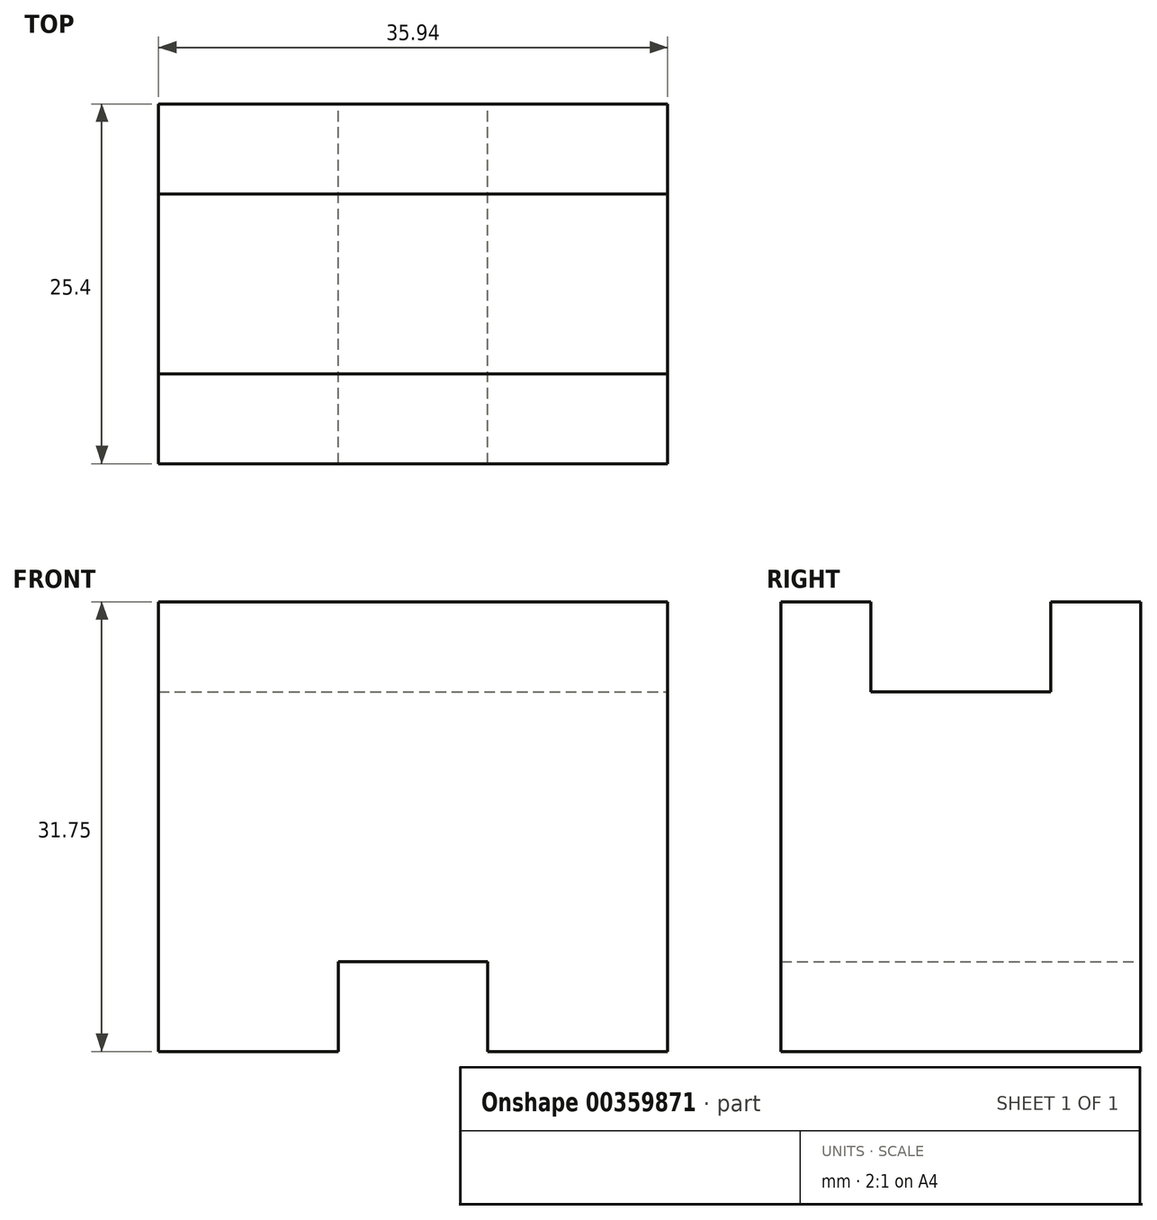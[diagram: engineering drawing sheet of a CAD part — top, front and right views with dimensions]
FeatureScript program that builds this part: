
annotation { "Feature Type Name" : "Feature", "Feature Type Description" : "" }
export const myFeature = defineFeature(function(context is Context, id is Id, definition is map)
    precondition{}
    {
        {
            var Q0;
            Q0=qCreatedBy(makeId("Front.planeOp"),FACE);
            var sketch = newSketch(context, id + "F0", { "sketchPlane" : qUnion([Q0])});
            skLineSegment(sketch, "E0", {"start": v(0, 0) * mm, "end": v(0, 31.75) * mm});
            skLineSegment(sketch, "E1", {"start": v(0, 31.75) * mm, "end": v(35.94, 31.75) * mm});
            skLineSegment(sketch, "E2", {"start": v(35.94, 31.75) * mm, "end": v(35.94, 0) * mm});
            skLineSegment(sketch, "E3", {"start": v(35.94, 0) * mm, "end": v(23.24, 0) * mm});
            skLineSegment(sketch, "E4", {"start": v(23.24, 0) * mm, "end": v(23.24, 6.35) * mm});
            skLineSegment(sketch, "E5", {"start": v(23.24, 6.35) * mm, "end": v(12.7, 6.35) * mm});
            skLineSegment(sketch, "E6", {"start": v(12.7, 6.35) * mm, "end": v(12.7, 0) * mm});
            skLineSegment(sketch, "E7", {"start": v(12.7, 0) * mm, "end": v(0, 0) * mm});
            skSolve(sketch);
        }
        {
            var Q0;
            Q0 = qSketchRegion(id + "F0", true);
            extrude(context, id + "F1", {"entities" : qUnion([Q0]), "depth" : 25.4 * mm});
        }
        {
            var Q0;
            Q0=makeQuery(id+"F1.opExtrude","SWEPT_FACE",FACE,{"disambiguationData":[OSD([sQuery(id+"F0.wireOp",EDGE,"E2")])]});
            var sketch = newSketch(context, id + "F2", { "sketchPlane" : qUnion([Q0])});
            skLineSegment(sketch, "E8", {"start": v(-19.05, 31.75) * mm, "end": v(-19.05, 25.4) * mm});
            skLineSegment(sketch, "E9", {"start": v(-19.05, 25.4) * mm, "end": v(-6.35, 25.4) * mm});
            skLineSegment(sketch, "E10", {"start": v(-6.35, 25.4) * mm, "end": v(-6.35, 31.75) * mm});
            skLineSegment(sketch, "E11", {"start": v(-19.05, 31.75) * mm, "end": v(-6.35, 31.75) * mm});
            skSolve(sketch);
        }
        {
            var Q0;
            Q0 = qSketchRegion(id + "F2", true);
            extrude(context, id + "F3", {"entities" : qUnion([Q0]), "operationType" : NewBodyOperationType.REMOVE, "oppositeDirection" : true, "depth" : 38.1 * mm});
        }
    });
